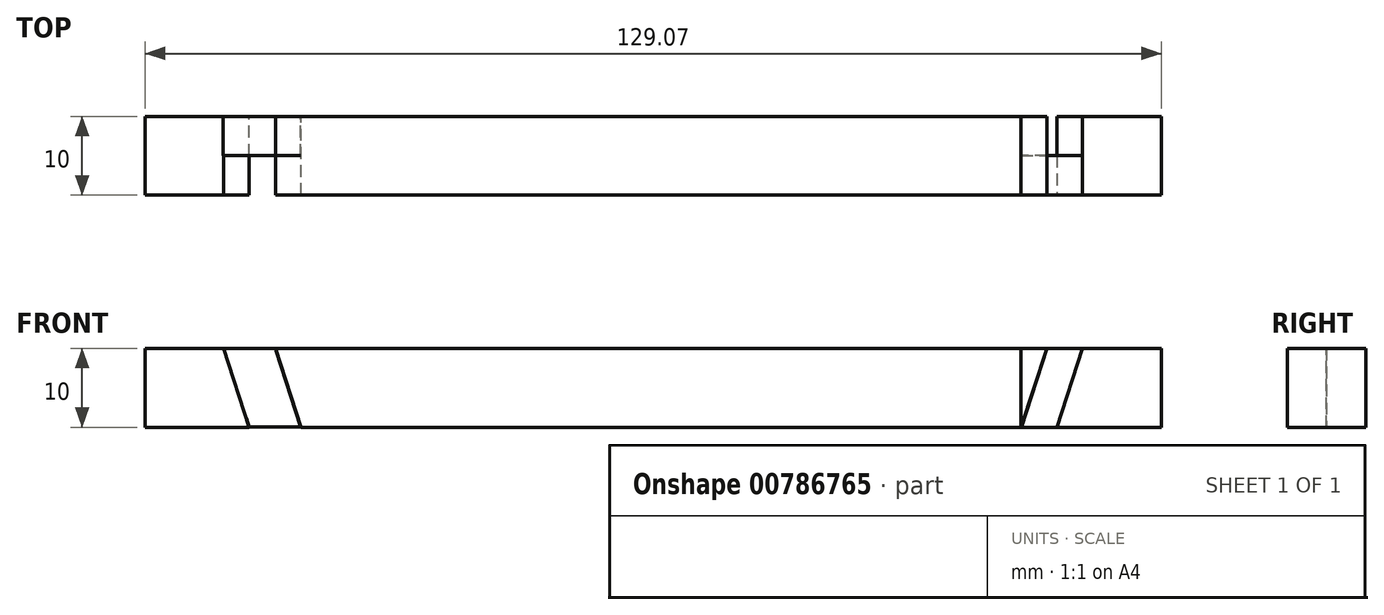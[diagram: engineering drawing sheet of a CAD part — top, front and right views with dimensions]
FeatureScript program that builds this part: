
annotation { "Feature Type Name" : "Feature", "Feature Type Description" : "" }
export const myFeature = defineFeature(function(context is Context, id is Id, definition is map)
    precondition{}
    {
        {
            var Q0;
            Q0=qCreatedBy(makeId("Front.planeOp"),FACE);
            var sketch = newSketch(context, id + "F0", { "sketchPlane" : qUnion([Q0])});
            skLineSegment(sketch, "E0", {"start": v(-68.13, 14.07) * mm, "end": v(-68.13, 4.07) * mm});
            skLineSegment(sketch, "E1", {"start": v(43.13, 4.07) * mm, "end": v(43.13, 14.07) * mm});
            skLineSegment(sketch, "E2", {"start": v(43.13, 14.07) * mm, "end": v(-51.58, 14.07) * mm});
            skLineSegment(sketch, "E3", {"start": v(-51.58, 14.07) * mm, "end": v(-48.34, 4.07) * mm});
            skLineSegment(sketch, "E4", {"start": v(-58.17, 14.07) * mm, "end": v(-68.13, 14.07) * mm});
            skLineSegment(sketch, "E5", {"start": v(-68.13, 4.07) * mm, "end": v(-54.88, 4.07) * mm});
            skLineSegment(sketch, "E6", {"start": v(-54.92, 4.07) * mm, "end": v(-58.17, 14.07) * mm});
            skLineSegment(sketch, "E7", {"start": v(-54.92, 4.07) * mm, "end": v(-54.88, 4.07) * mm});
            skLineSegment(sketch, "E8", {"start": v(-48.34, 4.07) * mm, "end": v(-48.34, 4.07) * mm});
            skLineSegment(sketch, "E9", {"start": v(-48.34, 4.07) * mm, "end": v(43.13, 4.07) * mm});
            skSolve(sketch);
        }
        {
            var Q0;
            Q0=makeQuery(id+"F0.imprint","IMPRINT",FACE,{"disambiguationData":[TD([[makeQuery(id+"F0.imprint","IMPRINT",EDGE,{"derivedFrom":sQuery(id+"F0.wireOp",EDGE,"E0")}),1.0]])]});
            var Q1;
            {var subQ0=sQuery(id+"F0.wireOp",EDGE,"E1");Q1=makeQuery(id+"F0.imprint","IMPRINT",FACE,{"disambiguationData":[TD([[makeQuery(id+"F0.imprint","IMPRINT",EDGE,{"derivedFrom":subQ0}),1.0]])]});}
            extrude(context, id + "F1", {"entities" : qUnion([Q0, Q1]), "depth" : 10 * mm, "offsetDistance" : 25 * mm});
        }
        {
            var Q0;
            Q0=makeQuery(id+"F0.imprint","IMPRINT",FACE,{"disambiguationData":[TD([[makeQuery(id+"F0.imprint","IMPRINT",EDGE,{"derivedFrom":sQuery(id+"F0.wireOp",EDGE,"E0")}),1.0]])]});
            var sketch = newSketch(context, id + "F2", { "sketchPlane" : qUnion([Q0])});
            skLineSegment(sketch, "E10", {"start": v(-54.91, 4.07) * mm, "end": v(-48.4, 4.07) * mm});
            skLineSegment(sketch, "E11", {"start": v(-48.4, 4.07) * mm, "end": v(-51.58, 14.07) * mm});
            skLineSegment(sketch, "E12", {"start": v(-51.58, 14.07) * mm, "end": v(-58.22, 14.07) * mm});
            skLineSegment(sketch, "E13", {"start": v(-58.22, 14.07) * mm, "end": v(-54.91, 4.07) * mm});
            skSolve(sketch);
        }
        {
            var Q0;
            {var subQ4=sQuery(id+"F2.wireOp",EDGE,"E10");Q0=makeQuery(id+"F2.imprint","IMPRINT",FACE,{"disambiguationData":[TD([[makeQuery(id+"F2.imprint","IMPRINT",EDGE,{"derivedFrom":subQ4}),1.0]])]});}
            var Q1;
            Q1 = qSketchRegion(id + "F2", true);
            extrude(context, id + "F3", {"entities" : qUnion([Q0, Q1]), "depth" : 5 * mm, "offsetDistance" : 25 * mm});
        }
        {
            var Q0;
            Q0=makeQuery(id+"F0.imprint","IMPRINT",FACE,{"disambiguationData":[TD([[makeQuery(id+"F0.imprint","IMPRINT",EDGE,{"derivedFrom":sQuery(id+"F0.wireOp",EDGE,"E1")}),1.0]])]});
            var sketch = newSketch(context, id + "F4", { "sketchPlane" : qUnion([Q0])});
            skLineSegment(sketch, "E14.bottom", {"start": v(43.13, 14.07) * mm, "end": v(46.38, 14.07) * mm});
            skLineSegment(sketch, "E14.top", {"start": v(43.13, 4.07) * mm, "end": v(43.13, 4.07) * mm});
            skLineSegment(sketch, "E14.left", {"start": v(43.13, 14.07) * mm, "end": v(43.13, 4.07) * mm});
            skLineSegment(sketch, "E14.right", {"start": v(60.94, 14.07) * mm, "end": v(60.94, 4.07) * mm});
            skLineSegment(sketch, "E15", {"start": v(46.38, 14.07) * mm, "end": v(43.13, 4.07) * mm});
            skLineSegment(sketch, "E16", {"start": v(50.94, 14.07) * mm, "end": v(47.7, 4.07) * mm});
            skLineSegment(sketch, "E17", {"start": v(50.94, 14.07) * mm, "end": v(60.94, 14.07) * mm});
            skLineSegment(sketch, "E18", {"start": v(47.7, 4.07) * mm, "end": v(60.94, 4.07) * mm});
            skSolve(sketch);
        }
        {
            var Q0;
            Q0=makeQuery(id+"F4.imprint","IMPRINT",FACE,{"disambiguationData":[TD([[makeQuery(id+"F4.imprint","IMPRINT",EDGE,{"derivedFrom":sQuery(id+"F4.wireOp",EDGE,"E14.right")}),-1.0]])]});
            var Q1;
            Q1=makeQuery(id+"F4.imprint","IMPRINT",FACE,{"disambiguationData":[TD([[makeQuery(id+"F4.imprint","IMPRINT",EDGE,{"derivedFrom":sQuery(id+"F4.wireOp",EDGE,"E14.bottom")}),-1.0]])]});
            extrude(context, id + "F5", {"entities" : qUnion([Q0, Q1]), "depth" : 10 * mm, "offsetDistance" : 25 * mm});
        }
        {
            var Q0;
            Q0=makeQuery(id+"F5.opExtrude","CAP_FACE",FACE,{"disambiguationData":[OSD([sQuery(id+"F4.wireOp",EDGE,"E14.right"),sQuery(id+"F4.wireOp",EDGE,"E16"),sQuery(id+"F4.wireOp",EDGE,"E17"),sQuery(id+"F4.wireOp",EDGE,"E18")])],"isStart":false});
            var sketch = newSketch(context, id + "F6", { "sketchPlane" : qUnion([Q0])});
            skLineSegment(sketch, "E19", {"start": v(50.94, 14.07) * mm, "end": v(46.4, 14.07) * mm});
            skLineSegment(sketch, "E20", {"start": v(46.4, 14.07) * mm, "end": v(43.15, 4.07) * mm});
            skLineSegment(sketch, "E21", {"start": v(43.15, 4.07) * mm, "end": v(47.7, 4.07) * mm});
            skLineSegment(sketch, "E22", {"start": v(47.7, 4.07) * mm, "end": v(50.94, 14.07) * mm});
            skSolve(sketch);
        }
        {
            var Q0;
            Q0=makeQuery(id+"F6.imprint","IMPRINT",FACE,{"disambiguationData":[TD([[makeQuery(id+"F6.imprint","IMPRINT",EDGE,{"derivedFrom":sQuery(id+"F6.wireOp",EDGE,"E19")}),1.0]])]});
            extrude(context, id + "F7", {"entities" : qUnion([Q0]), "oppositeDirection" : true, "depth" : 5 * mm, "offsetDistance" : 25 * mm});
        }
    });
